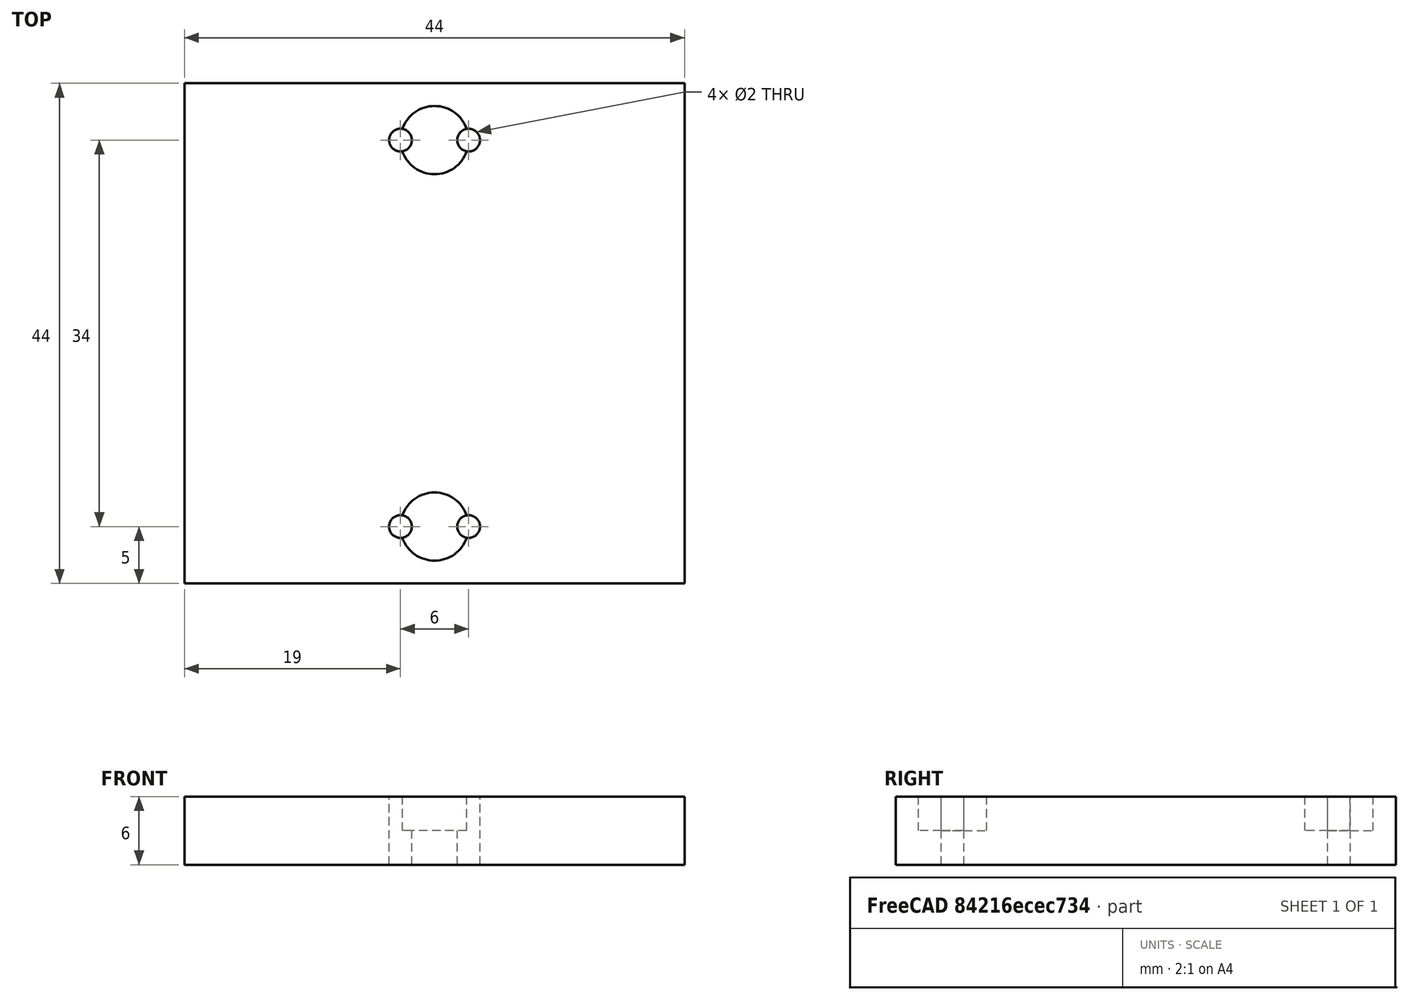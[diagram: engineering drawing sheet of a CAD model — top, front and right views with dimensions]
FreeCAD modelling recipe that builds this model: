
FCSTD DOCUMENT  (FreeCAD 0.16R)
Label: bottom-part
License: All rights reserved
LicenseURL: http://en.wikipedia.org/wiki/All_rights_reserved
objects: Part::Cylinder×6, Part::Cut×6, Part::Box×1
note: 13 computed .brp shape members not serialized (recipe doc carries the construction recipe); baked Part::Feature solids carry a one-line shape summary decoded from their .brp

FEATURE [Part::Box] Box  label="Cube"
  Height = 6
  Length = 44
  Width = 44
FEATURE [Part::Cylinder] Cylinder
  Angle = 360
  Height = 10
  Placement = pos=(22,5,3) rot=(0,0,1;0rad)
  Radius = 3
FEATURE [Part::Cylinder] Cylinder001
  Angle = 360
  Height = 10
  Placement = pos=(22,39,3) rot=(0,0,1;0rad)
  Radius = 3
FEATURE [Part::Cut] Cut
  Base = -> Box
  Tool = -> Cylinder001
FEATURE [Part::Cut] Cut001
  Base = -> Cut
  Tool = -> Cylinder
FEATURE [Part::Cylinder] Cylinder002
  Angle = 360
  Height = 10
  Placement = pos=(19,5,-2) rot=(0,0,1;0rad)
  Radius = 1
FEATURE [Part::Cylinder] Cylinder003
  Angle = 360
  Height = 10
  Placement = pos=(25,5,-2) rot=(0,0,1;0rad)
  Radius = 1
FEATURE [Part::Cylinder] Cylinder004
  Angle = 360
  Height = 10
  Placement = pos=(19,39,-2) rot=(0,0,1;0rad)
  Radius = 1
FEATURE [Part::Cylinder] Cylinder005
  Angle = 360
  Height = 10
  Placement = pos=(25,39,-2) rot=(0,0,1;0rad)
  Radius = 1
FEATURE [Part::Cut] Cut002
  Base = -> Cut001
  Tool = -> Cylinder002
FEATURE [Part::Cut] Cut003
  Base = -> Cut002
  Tool = -> Cylinder003
FEATURE [Part::Cut] Cut004
  Base = -> Cut003
  Tool = -> Cylinder005
FEATURE [Part::Cut] Cut005
  Base = -> Cut004
  Tool = -> Cylinder004
